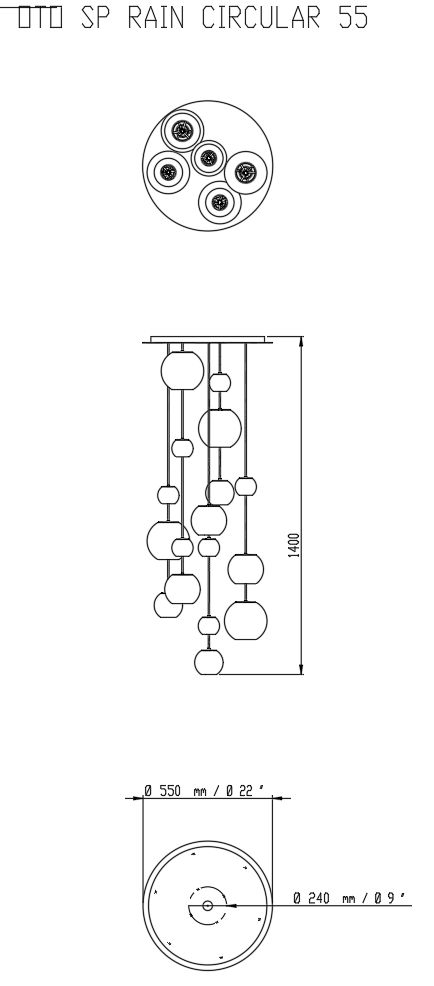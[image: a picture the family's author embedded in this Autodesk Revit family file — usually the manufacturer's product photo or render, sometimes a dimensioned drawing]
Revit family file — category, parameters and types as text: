
# Revit family: OTO-Suspension
name_source: partatom
category: Lighting Fixtures
units: mm (PartAtom-declared; Revit-internal decimal feet)

## family parameters
Always vertical = Yes
Cut with Voids When Loaded = No
Host = Ceiling
Light Source = No
OmniClass Number = 23.80.70.11
OmniClass Title = Luminaries for Internal Lighting
Part Type = Junction Box
Room Calculation Point = No
Round Connector Dimension = Use Diameter
Shared = No

## types (16) — shared parameters
Bulb Diametr = 15 mm  [stored 0.0492126 ft]
Country = Europe
Description = SUSPENSION
Designer = Pio e Tito Toso
Manufacturer = Vistosi
Manufacturer country = Italy
Model = OTO
Type Comments = Pio e Tito Toso
URL = https://vistosi.com
URL Product Page = https://vistosi.it
zero-valued in all types: Default Elevation

## per-type parameters (varying)
| type | Depth | Lampshade Type | OTO SP Base (Small) | OTO SP12-15 | Width |
| OTO SP 12 | 0 mm  [stored 0 ft] | Oto_Lampshade : OTO_H=100mm D=120mm | Yes | Yes | 12 mm  [stored 0.0393701 ft] |
| OTO SP 15 | 0 mm  [stored 0 ft] | Oto_Lampshade : OTO_H=120mm D=150mm | Yes | Yes | 15 mm  [stored 0.0492126 ft] |
| OTO SP 18 | 0 mm  [stored 0 ft] | Oto_Lampshade : OTO_H=160mm D=180mm | Yes | Yes | 18 mm  [stored 0.0590551 ft] |
| OTO SP CHANDELIER | 0 mm  [stored 0 ft] | Oto_Lampshade : OTO_H=160mm D=180mm | No | No | 140 mm  [stored 0.459318 ft] |
| OTO SP CUBE | 80 mm  [stored 0.262467 ft] | Oto_Lampshade : OTO_H=160mm D=180mm | No | No | 80 mm  [stored 0.262467 ft] |
| OTO SP FLYING CARPET | 76 mm  [stored 0.249344 ft] | Oto_Lampshade : OTO_H=160mm D=180mm | No | No | 169 mm  [stored 0.554462 ft] |
| OTO SP LINEAR | 18 mm  [stored 0.0590551 ft] | Oto_Lampshade : OTO_H=160mm D=180mm | No | No | 120 mm  [stored 0.393701 ft] |
| OTO SP PEARL | 0 mm  [stored 0 ft] | Oto_Lampshade : OTO_H=160mm D=180mm | Yes | No | 15 mm  [stored 0.0492126 ft] |
| OTO SP PEARL C | 0 mm  [stored 0 ft] | Oto_Lampshade : OTO_H=160mm D=180mm | Yes | No | 15 mm  [stored 0.0492126 ft] |
| OTO SP PEARL D | 0 mm  [stored 0 ft] | Oto_Lampshade : OTO_H=160mm D=180mm | Yes | No | 15 mm  [stored 0.0492126 ft] |
| OTO SP PEARL B | 0 mm  [stored 0 ft] | Oto_Lampshade : OTO_H=160mm D=180mm | Yes | No | 15 mm  [stored 0.0492126 ft] |
| OTO SP R60 | 0 mm  [stored 0 ft] | Oto_Lampshade : OTO_H=160mm D=180mm | No | No | 60 mm  [stored 0.19685 ft] |
| OTO SP RAIN CIRCULAR 55 | 0 mm  [stored 0 ft] | Oto_Lampshade : OTO_H=160mm D=180mm | No | No | 60 mm  [stored 0.19685 ft] |
| OTO SP RAIN CIRCLE | 0 mm  [stored 0 ft] | Oto_Lampshade : OTO_H=160mm D=180mm | No | No | 60 mm  [stored 0.19685 ft] |
| OTO SP SURFACE | 108 mm  [stored 0.354331 ft] | Oto_Lampshade : OTO_H=160mm D=180mm | No | No | 108 mm  [stored 0.354331 ft] |
| OTO SP SPHERE | 0 mm  [stored 0 ft] | Oto_Lampshade : OTO_H=160mm D=180mm | No | No | 100 mm  [stored 0.328084 ft] |

type visibility flags (boolean, named after types; folded from table):
- OTO SP 12: Yes: (none)
- OTO SP 15: Yes: (none)
- OTO SP 18: Yes: (none)
- OTO SP CHANDELIER: Yes: OTO SP CHANDELIER
- OTO SP CUBE: Yes: OTO SP CUBE
- OTO SP FLYING CARPET: Yes: OTO SP FLYING CARPET
- OTO SP LINEAR: Yes: OTO SP LINEAR
- OTO SP PEARL: Yes: OTO SP PEARL
- OTO SP PEARL C: Yes: OTO SP PEARL C
- OTO SP PEARL D: Yes: OTO SP PEARL D
- OTO SP PEARL B: Yes: OTO SP PEARL B
- OTO SP R60: Yes: OTO SP R60
- OTO SP RAIN CIRCULAR 55: Yes: OTO SP RAIN CIRCULAR 55
- OTO SP RAIN CIRCLE: Yes: OTO SP RAIN CIRCLE
- OTO SP SURFACE: Yes: OTO SP SURFACE
- OTO SP SPHERE: Yes: OTO SP SPHERE

note: [stored X ft] marks values corroborated as IEEE doubles in the binary element streams (Revit-internal decimal feet)

## geometry (parser evidence)
native form markers: Sweep x12
no freeform markers — native parametric forms only
